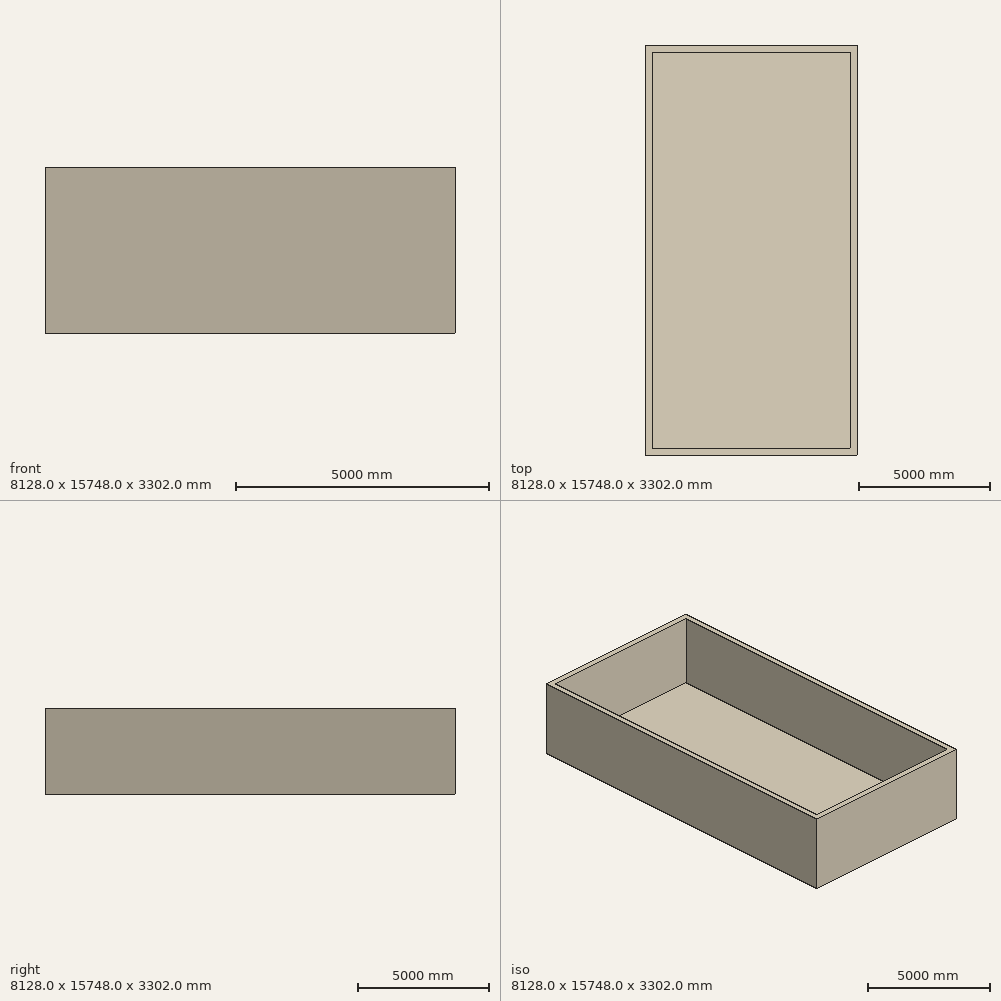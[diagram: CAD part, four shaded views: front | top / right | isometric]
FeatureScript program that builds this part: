
annotation { "Feature Type Name" : "Feature", "Feature Type Description" : "" }
export const myFeature = defineFeature(function(context is Context, id is Id, definition is map)
    precondition{}
    {
        {
            var Q0;
            Q0=qCreatedBy(makeId("Top.planeOp"),FACE);
            var sketch = newSketch(context, id + "F0", { "sketchPlane" : qUnion([Q0])});
            skLineSegment(sketch, "E0.bottom", {"start": v(4064, -7874) * mm, "end": v(-4064, -7874) * mm});
            skLineSegment(sketch, "E0.top", {"start": v(4064, 7874) * mm, "end": v(-4064, 7874) * mm});
            skLineSegment(sketch, "E0.left", {"start": v(4064, -7874) * mm, "end": v(4064, 7874) * mm});
            skLineSegment(sketch, "E0.right", {"start": v(-4064, -7874) * mm, "end": v(-4064, 7874) * mm});
            skPoint(sketch, "E0.middle", {"position": v(0, 0) * mm});
            skSolve(sketch);
        }
        {
            var Q0;
            Q0=qSketchRegion(id+"F0",true);
            extrude(context, id + "F1", {"entities" : qUnion([Q0]), "oppositeDirection" : true, "depth" : 254 * mm, "offsetDistance" : 25.4 * mm});
        }
        {
            var Q0;
            Q0=makeQuery(id+"F1.opExtrude","CAP_FACE",FACE,{"disambiguationData":[OSD([sQuery(id+"F0.wireOp",EDGE,"E0.bottom"),sQuery(id+"F0.wireOp",EDGE,"E0.top"),sQuery(id+"F0.wireOp",EDGE,"E0.left"),sQuery(id+"F0.wireOp",EDGE,"E0.right")])],"isStart":true});
            var sketch = newSketch(context, id + "F2", { "sketchPlane" : qUnion([Q0])});
            skLineSegment(sketch, "E1.0", {"start": v(3810, -7620) * mm, "end": v(-3810, -7620) * mm});
            skLineSegment(sketch, "E1.1", {"start": v(3810, -7620) * mm, "end": v(3810, 7620) * mm});
            skLineSegment(sketch, "E1.2", {"start": v(3810, 7620) * mm, "end": v(-3810, 7620) * mm});
            skLineSegment(sketch, "E1.3", {"start": v(-3810, -7620) * mm, "end": v(-3810, 7620) * mm});
            skSolve(sketch);
        }
        {
            var Q0;
            Q0=makeQuery(id+"F2.imprint","IMPRINT",FACE,{"disambiguationData":[TD([[makeQuery(id+"F2.imprint","IMPRINT",EDGE,{"derivedFrom":sQuery(id+"F2.wireOp",EDGE,"E1.0")}),1.0]])]});
            extrude(context, id + "F3", {"entities" : qUnion([Q0]), "operationType" : NewBodyOperationType.ADD, "depth" : 3048 * mm, "offsetDistance" : 25.4 * mm});
        }
    });
